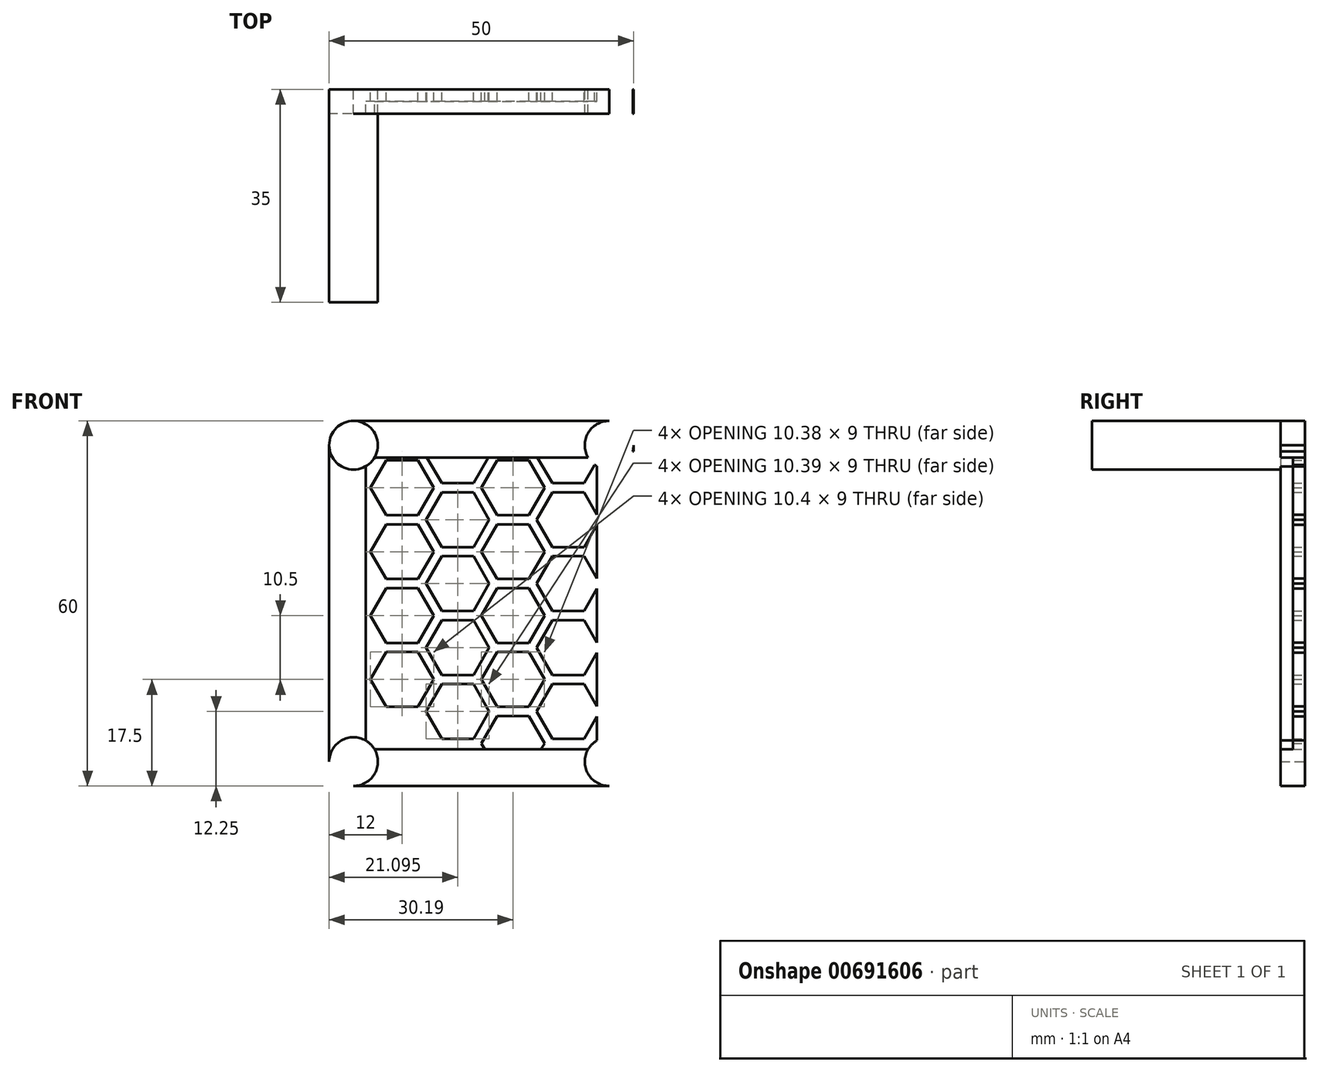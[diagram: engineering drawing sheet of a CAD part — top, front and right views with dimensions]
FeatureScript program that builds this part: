
annotation { "Feature Type Name" : "Feature", "Feature Type Description" : "" }
export const myFeature = defineFeature(function(context is Context, id is Id, definition is map)
    precondition{}
    {
        {
            var Q0;
            Q0=qCreatedBy(makeId("Front.planeOp"),FACE);
            var sketch = newSketch(context, id + "F0", { "sketchPlane" : qUnion([Q0])});
            skLineSegment(sketch, "E0.bottom", {"start": v(-21, 30) * mm, "end": v(21, 30) * mm});
            skLineSegment(sketch, "E0.top", {"start": v(-21, -30) * mm, "end": v(21, -30) * mm});
            skLineSegment(sketch, "E0.left", {"start": v(-25, 26) * mm, "end": v(-25, -26) * mm});
            skLineSegment(sketch, "E0.right", {"start": v(25, 26) * mm, "end": v(25, -26) * mm});
            skPoint(sketch, "E0.middle", {"position": v(0, 0) * mm});
            skCircle(sketch, "E1", {"center": v(-21, 26) * mm, "radius": 4 * mm});
            skPoint(sketch, "E2.visualSharp", {"position": v(-25, 30) * mm});
            skArc(sketch, "E2.filletArc", {"start": v(-21, 30) * mm, "mid": v(-23.83, 28.83) * mm, "end": v(-25, 26) * mm});
            skPoint(sketch, "E3.visualSharp", {"position": v(25, 30) * mm});
            skArc(sketch, "E3.filletArc", {"start": v(25, 26) * mm, "mid": v(23.83, 28.83) * mm, "end": v(21, 30) * mm});
            skPoint(sketch, "E4.visualSharp", {"position": v(25, -30) * mm});
            skArc(sketch, "E4.filletArc", {"start": v(21, -30) * mm, "mid": v(23.83, -28.83) * mm, "end": v(25, -26) * mm});
            skPoint(sketch, "E5.visualSharp", {"position": v(-25, -30) * mm});
            skArc(sketch, "E5.filletArc", {"start": v(-25, -26) * mm, "mid": v(-23.83, -28.83) * mm, "end": v(-21, -30) * mm});
            skLineSegment(sketch, "E6", {"start": v(-17.54, 24) * mm, "end": v(17.54, 24) * mm});
            skLineSegment(sketch, "E7", {"start": v(-17.54, -24) * mm, "end": v(17.54, -24) * mm});
            skLineSegment(sketch, "E8", {"start": v(19, 22.54) * mm, "end": v(19, -22.54) * mm});
            skLineSegment(sketch, "E9", {"start": v(-19, 22.54) * mm, "end": v(-19, -22.54) * mm});
            skCircle(sketch, "E10.cCircle", {"center": v(-13, 19) * mm, "radius": 4.5 * mm, "construction": true});
            skLineSegment(sketch, "E10.0", {"start": v(-7.8, 19) * mm, "end": v(-10.4, 14.5) * mm});
            skLineSegment(sketch, "E10.1", {"start": v(-10.4, 14.5) * mm, "end": v(-15.6, 14.5) * mm});
            skLineSegment(sketch, "E10.2", {"start": v(-15.6, 14.5) * mm, "end": v(-18.2, 19) * mm});
            skLineSegment(sketch, "E10.3", {"start": v(-18.2, 19) * mm, "end": v(-15.6, 23.5) * mm});
            skLineSegment(sketch, "E10.4", {"start": v(-15.6, 23.5) * mm, "end": v(-10.4, 23.5) * mm});
            skLineSegment(sketch, "E10.5", {"start": v(-10.4, 23.5) * mm, "end": v(-7.8, 19) * mm});
            skPoint(sketch, "E10.0.midPoint", {"position": v(-9.1, 16.75) * mm});
            skLineSegment(sketch, "E11.0.1.0", {"start": v(-10.4, 4) * mm, "end": v(-15.6, 4) * mm});
            skLineSegment(sketch, "E11.0.1.1", {"start": v(-7.8, 8.5) * mm, "end": v(-10.4, 4) * mm});
            skLineSegment(sketch, "E11.0.1.2", {"start": v(-10.4, 13) * mm, "end": v(-7.8, 8.5) * mm});
            skLineSegment(sketch, "E11.0.1.3", {"start": v(-15.6, 13) * mm, "end": v(-10.4, 13) * mm});
            skLineSegment(sketch, "E11.0.1.4", {"start": v(-18.2, 8.5) * mm, "end": v(-15.6, 13) * mm});
            skLineSegment(sketch, "E11.0.1.5", {"start": v(-15.6, 4) * mm, "end": v(-18.2, 8.5) * mm});
            skLineSegment(sketch, "E11.0.2.0", {"start": v(-10.4, -6.5) * mm, "end": v(-15.6, -6.5) * mm});
            skLineSegment(sketch, "E11.0.2.1", {"start": v(-7.8, -2) * mm, "end": v(-10.4, -6.5) * mm});
            skLineSegment(sketch, "E11.0.2.2", {"start": v(-10.4, 2.5) * mm, "end": v(-7.8, -2) * mm});
            skLineSegment(sketch, "E11.0.2.3", {"start": v(-15.6, 2.5) * mm, "end": v(-10.4, 2.5) * mm});
            skLineSegment(sketch, "E11.0.2.4", {"start": v(-18.2, -2) * mm, "end": v(-15.6, 2.5) * mm});
            skLineSegment(sketch, "E11.0.2.5", {"start": v(-15.6, -6.5) * mm, "end": v(-18.2, -2) * mm});
            skLineSegment(sketch, "E11.0.3.0", {"start": v(-10.4, -17) * mm, "end": v(-15.6, -17) * mm});
            skLineSegment(sketch, "E11.0.3.1", {"start": v(-7.8, -12.5) * mm, "end": v(-10.4, -17) * mm});
            skLineSegment(sketch, "E11.0.3.2", {"start": v(-10.4, -8) * mm, "end": v(-7.8, -12.5) * mm});
            skLineSegment(sketch, "E11.0.3.3", {"start": v(-15.6, -8) * mm, "end": v(-10.4, -8) * mm});
            skLineSegment(sketch, "E11.0.3.4", {"start": v(-18.2, -12.5) * mm, "end": v(-15.6, -8) * mm});
            skLineSegment(sketch, "E11.0.3.5", {"start": v(-15.6, -17) * mm, "end": v(-18.2, -12.5) * mm});
            skLineSegment(sketch, "E11.0.4.1", {"start": v(-7.8, -23) * mm, "end": v(-10.4, -27.5) * mm});
            skLineSegment(sketch, "E11.0.4.2", {"start": v(-10.4, -18.5) * mm, "end": v(-7.8, -23) * mm});
            skLineSegment(sketch, "E11.0.4.3", {"start": v(-15.6, -18.5) * mm, "end": v(-10.4, -18.5) * mm});
            skLineSegment(sketch, "E11.0.4.4", {"start": v(-18.2, -23) * mm, "end": v(-15.6, -18.5) * mm});
            skLineSegment(sketch, "E11.1.0.0", {"start": v(-1.3, 19.75) * mm, "end": v(-6.5, 19.75) * mm});
            skLineSegment(sketch, "E11.1.0.1", {"start": v(1.29, 24.25) * mm, "end": v(-1.3, 19.75) * mm});
            skLineSegment(sketch, "E11.1.0.5", {"start": v(-6.5, 19.75) * mm, "end": v(-9.1, 24.25) * mm});
            skLineSegment(sketch, "E11.1.1.0", {"start": v(-1.3, 9.25) * mm, "end": v(-6.5, 9.25) * mm});
            skLineSegment(sketch, "E11.1.1.1", {"start": v(1.29, 13.75) * mm, "end": v(-1.3, 9.25) * mm});
            skLineSegment(sketch, "E11.1.1.2", {"start": v(-1.3, 18.25) * mm, "end": v(1.29, 13.75) * mm});
            skLineSegment(sketch, "E11.1.1.3", {"start": v(-6.5, 18.25) * mm, "end": v(-1.3, 18.25) * mm});
            skLineSegment(sketch, "E11.1.1.4", {"start": v(-9.1, 13.75) * mm, "end": v(-6.5, 18.25) * mm});
            skLineSegment(sketch, "E11.1.1.5", {"start": v(-6.5, 9.25) * mm, "end": v(-9.1, 13.75) * mm});
            skLineSegment(sketch, "E11.1.2.0", {"start": v(-1.3, -1.25) * mm, "end": v(-6.5, -1.25) * mm});
            skLineSegment(sketch, "E11.1.2.1", {"start": v(1.29, 3.25) * mm, "end": v(-1.3, -1.25) * mm});
            skLineSegment(sketch, "E11.1.2.2", {"start": v(-1.3, 7.75) * mm, "end": v(1.29, 3.25) * mm});
            skLineSegment(sketch, "E11.1.2.3", {"start": v(-6.5, 7.75) * mm, "end": v(-1.3, 7.75) * mm});
            skLineSegment(sketch, "E11.1.2.4", {"start": v(-9.1, 3.25) * mm, "end": v(-6.5, 7.75) * mm});
            skLineSegment(sketch, "E11.1.2.5", {"start": v(-6.5, -1.25) * mm, "end": v(-9.1, 3.25) * mm});
            skLineSegment(sketch, "E11.1.3.0", {"start": v(-1.3, -11.75) * mm, "end": v(-6.5, -11.75) * mm});
            skLineSegment(sketch, "E11.1.3.1", {"start": v(1.29, -7.25) * mm, "end": v(-1.3, -11.75) * mm});
            skLineSegment(sketch, "E11.1.3.2", {"start": v(-1.3, -2.75) * mm, "end": v(1.29, -7.25) * mm});
            skLineSegment(sketch, "E11.1.3.3", {"start": v(-6.5, -2.75) * mm, "end": v(-1.3, -2.75) * mm});
            skLineSegment(sketch, "E11.1.3.4", {"start": v(-9.1, -7.25) * mm, "end": v(-6.5, -2.75) * mm});
            skLineSegment(sketch, "E11.1.3.5", {"start": v(-6.5, -11.75) * mm, "end": v(-9.1, -7.25) * mm});
            skLineSegment(sketch, "E11.1.4.0", {"start": v(-1.3, -22.25) * mm, "end": v(-6.5, -22.25) * mm});
            skLineSegment(sketch, "E11.1.4.1", {"start": v(1.29, -17.75) * mm, "end": v(-1.3, -22.25) * mm});
            skLineSegment(sketch, "E11.1.4.2", {"start": v(-1.3, -13.25) * mm, "end": v(1.29, -17.75) * mm});
            skLineSegment(sketch, "E11.1.4.3", {"start": v(-6.5, -13.25) * mm, "end": v(-1.3, -13.25) * mm});
            skLineSegment(sketch, "E11.1.4.4", {"start": v(-9.1, -17.75) * mm, "end": v(-6.5, -13.25) * mm});
            skLineSegment(sketch, "E11.1.4.5", {"start": v(-6.5, -22.25) * mm, "end": v(-9.1, -17.75) * mm});
            skLineSegment(sketch, "E11.2.1.0", {"start": v(7.78, 14.5) * mm, "end": v(2.59, 14.5) * mm});
            skLineSegment(sketch, "E11.2.1.1", {"start": v(10.38, 19) * mm, "end": v(7.78, 14.5) * mm});
            skLineSegment(sketch, "E11.2.1.2", {"start": v(7.78, 23.5) * mm, "end": v(10.38, 19) * mm});
            skLineSegment(sketch, "E11.2.1.3", {"start": v(2.59, 23.5) * mm, "end": v(7.78, 23.5) * mm});
            skLineSegment(sketch, "E11.2.1.4", {"start": v(0, 19) * mm, "end": v(2.59, 23.5) * mm});
            skLineSegment(sketch, "E11.2.1.5", {"start": v(2.59, 14.5) * mm, "end": v(0, 19) * mm});
            skLineSegment(sketch, "E11.2.2.0", {"start": v(7.78, 4) * mm, "end": v(2.59, 4) * mm});
            skLineSegment(sketch, "E11.2.2.1", {"start": v(10.38, 8.5) * mm, "end": v(7.78, 4) * mm});
            skLineSegment(sketch, "E11.2.2.2", {"start": v(7.78, 13) * mm, "end": v(10.38, 8.5) * mm});
            skLineSegment(sketch, "E11.2.2.3", {"start": v(2.59, 13) * mm, "end": v(7.78, 13) * mm});
            skLineSegment(sketch, "E11.2.2.4", {"start": v(0, 8.5) * mm, "end": v(2.59, 13) * mm});
            skLineSegment(sketch, "E11.2.2.5", {"start": v(2.59, 4) * mm, "end": v(0, 8.5) * mm});
            skLineSegment(sketch, "E11.2.3.0", {"start": v(7.78, -6.5) * mm, "end": v(2.59, -6.5) * mm});
            skLineSegment(sketch, "E11.2.3.1", {"start": v(10.38, -2) * mm, "end": v(7.78, -6.5) * mm});
            skLineSegment(sketch, "E11.2.3.2", {"start": v(7.78, 2.5) * mm, "end": v(10.38, -2) * mm});
            skLineSegment(sketch, "E11.2.3.3", {"start": v(2.59, 2.5) * mm, "end": v(7.78, 2.5) * mm});
            skLineSegment(sketch, "E11.2.3.4", {"start": v(0, -2) * mm, "end": v(2.59, 2.5) * mm});
            skLineSegment(sketch, "E11.2.3.5", {"start": v(2.59, -6.5) * mm, "end": v(0, -2) * mm});
            skLineSegment(sketch, "E11.2.4.0", {"start": v(7.78, -17) * mm, "end": v(2.59, -17) * mm});
            skLineSegment(sketch, "E11.2.4.1", {"start": v(10.38, -12.5) * mm, "end": v(7.78, -17) * mm});
            skLineSegment(sketch, "E11.2.4.2", {"start": v(7.78, -8) * mm, "end": v(10.38, -12.5) * mm});
            skLineSegment(sketch, "E11.2.4.3", {"start": v(2.59, -8) * mm, "end": v(7.78, -8) * mm});
            skLineSegment(sketch, "E11.2.4.4", {"start": v(0, -12.5) * mm, "end": v(2.59, -8) * mm});
            skLineSegment(sketch, "E11.2.4.5", {"start": v(2.59, -17) * mm, "end": v(0, -12.5) * mm});
            skLineSegment(sketch, "E11.2.5.1", {"start": v(10.38, -23) * mm, "end": v(7.78, -27.5) * mm});
            skLineSegment(sketch, "E11.2.5.2", {"start": v(7.78, -18.5) * mm, "end": v(10.38, -23) * mm});
            skLineSegment(sketch, "E11.2.5.3", {"start": v(2.59, -18.5) * mm, "end": v(7.78, -18.5) * mm});
            skLineSegment(sketch, "E11.2.5.4", {"start": v(0, -23) * mm, "end": v(2.59, -18.5) * mm});
            skLineSegment(sketch, "E11.2.5.5", {"start": v(2.59, -27.5) * mm, "end": v(0, -23) * mm});
            skLineSegment(sketch, "E11.direction1", {"start": v(-15.6, 14.5) * mm, "end": v(-6.5, 19.75) * mm, "construction": true});
            skLineSegment(sketch, "E11.direction2", {"start": v(-15.6, 14.5) * mm, "end": v(-15.6, 4) * mm, "construction": true});
            skLineSegment(sketch, "E12.0.3.1", {"start": v(16.88, 19.75) * mm, "end": v(11.68, 19.75) * mm});
            skLineSegment(sketch, "E12.3.3.1", {"start": v(19.48, 24.25) * mm, "end": v(16.88, 19.75) * mm});
            skLineSegment(sketch, "E12.15.3.1", {"start": v(11.68, 19.75) * mm, "end": v(9.08, 24.25) * mm});
            skLineSegment(sketch, "E12.0.3.2", {"start": v(16.88, 9.25) * mm, "end": v(11.68, 9.25) * mm});
            skLineSegment(sketch, "E12.3.3.2", {"start": v(19.48, 13.75) * mm, "end": v(16.88, 9.25) * mm});
            skLineSegment(sketch, "E12.6.3.2", {"start": v(16.88, 18.25) * mm, "end": v(19.48, 13.75) * mm});
            skLineSegment(sketch, "E12.9.3.2", {"start": v(11.68, 18.25) * mm, "end": v(16.88, 18.25) * mm});
            skLineSegment(sketch, "E12.12.3.2", {"start": v(9.08, 13.75) * mm, "end": v(11.68, 18.25) * mm});
            skLineSegment(sketch, "E12.15.3.2", {"start": v(11.68, 9.25) * mm, "end": v(9.08, 13.75) * mm});
            skLineSegment(sketch, "E12.0.3.3", {"start": v(16.88, -1.25) * mm, "end": v(11.68, -1.25) * mm});
            skLineSegment(sketch, "E12.3.3.3", {"start": v(19.48, 3.25) * mm, "end": v(16.88, -1.25) * mm});
            skLineSegment(sketch, "E12.6.3.3", {"start": v(16.88, 7.75) * mm, "end": v(19.48, 3.25) * mm});
            skLineSegment(sketch, "E12.9.3.3", {"start": v(11.68, 7.75) * mm, "end": v(16.88, 7.75) * mm});
            skLineSegment(sketch, "E12.12.3.3", {"start": v(9.08, 3.25) * mm, "end": v(11.68, 7.75) * mm});
            skLineSegment(sketch, "E12.15.3.3", {"start": v(11.68, -1.25) * mm, "end": v(9.08, 3.25) * mm});
            skLineSegment(sketch, "E12.0.3.4", {"start": v(16.88, -11.75) * mm, "end": v(11.68, -11.75) * mm});
            skLineSegment(sketch, "E12.3.3.4", {"start": v(19.48, -7.25) * mm, "end": v(16.88, -11.75) * mm});
            skLineSegment(sketch, "E12.6.3.4", {"start": v(16.88, -2.75) * mm, "end": v(19.48, -7.25) * mm});
            skLineSegment(sketch, "E12.9.3.4", {"start": v(11.68, -2.75) * mm, "end": v(16.88, -2.75) * mm});
            skLineSegment(sketch, "E12.12.3.4", {"start": v(9.08, -7.25) * mm, "end": v(11.68, -2.75) * mm});
            skLineSegment(sketch, "E12.15.3.4", {"start": v(11.68, -11.75) * mm, "end": v(9.08, -7.25) * mm});
            skLineSegment(sketch, "E12.0.3.5", {"start": v(16.88, -22.25) * mm, "end": v(11.68, -22.25) * mm});
            skLineSegment(sketch, "E12.3.3.5", {"start": v(19.48, -17.75) * mm, "end": v(16.88, -22.25) * mm});
            skLineSegment(sketch, "E12.6.3.5", {"start": v(16.88, -13.25) * mm, "end": v(19.48, -17.75) * mm});
            skLineSegment(sketch, "E12.9.3.5", {"start": v(11.68, -13.25) * mm, "end": v(16.88, -13.25) * mm});
            skLineSegment(sketch, "E12.12.3.5", {"start": v(9.08, -17.75) * mm, "end": v(11.68, -13.25) * mm});
            skLineSegment(sketch, "E12.15.3.5", {"start": v(11.68, -22.25) * mm, "end": v(9.08, -17.75) * mm});
            skLineSegment(sketch, "E12.9.4.0", {"start": v(20.77, 44.5) * mm, "end": v(25.97, 44.5) * mm});
            skLineSegment(sketch, "E12.0.4.1", {"start": v(25.97, 25) * mm, "end": v(20.77, 25) * mm});
            skLineSegment(sketch, "E13", {"start": v(0, 40.96) * mm, "end": v(0, -40.98) * mm, "construction": true});
            skLineSegment(sketch, "E14", {"start": v(-42.2, 0) * mm, "end": v(47.65, 0) * mm, "construction": true});
            skCircle(sketch, "E15.MirrorC", {"center": v(21, 26) * mm, "radius": 4 * mm});
            skCircle(sketch, "E16.MirrorC", {"center": v(-21, -26) * mm, "radius": 4 * mm});
            skCircle(sketch, "E17.MirrorC", {"center": v(21, -26) * mm, "radius": 4 * mm});
            skSolve(sketch);
        }
        {
            var Q0;
            {var subQ3=sQuery(id+"F0.wireOp",EDGE,"E6");Q0=makeQuery(id+"F0.imprint","IMPRINT",FACE,{"disambiguationData":[TD([[makeQuery(id+"F0.imprint","IMPRINT",EDGE,{"derivedFrom":subQ3}),-1.0]])]});}
            extrude(context, id + "F1", {"entities" : qUnion([Q0]), "depth" : 2 * mm, "offsetDistance" : 25 * mm});
        }
        {
            var Q0;
            {var subQ0=sQuery(id+"F0.wireOp",EDGE,"E0.right");Q0=makeQuery(id+"F0.imprint","IMPRINT",FACE,{"disambiguationData":[TD([[makeQuery(id+"F0.imprint","IMPRINT",EDGE,{"derivedFrom":subQ0}),-1.0]])]});}
            var Q1;
            {var subQ0=sQuery(id+"F0.wireOp",EDGE,"E0.bottom");Q1=makeQuery(id+"F0.imprint","IMPRINT",FACE,{"disambiguationData":[TD([[makeQuery(id+"F0.imprint","IMPRINT",EDGE,{"derivedFrom":subQ0}),-1.0]])]});}
            var Q2;
            {var subQ0=sQuery(id+"F0.wireOp",EDGE,"E0.left");Q2=makeQuery(id+"F0.imprint","IMPRINT",FACE,{"disambiguationData":[TD([[makeQuery(id+"F0.imprint","IMPRINT",EDGE,{"derivedFrom":subQ0}),1.0]])]});}
            var Q3;
            {var subQ0=sQuery(id+"F0.wireOp",EDGE,"E0.top");Q3=makeQuery(id+"F0.imprint","IMPRINT",FACE,{"disambiguationData":[TD([[makeQuery(id+"F0.imprint","IMPRINT",EDGE,{"derivedFrom":subQ0}),1.0]])]});}
            extrude(context, id + "F2", {"entities" : qUnion([Q0, Q1, Q2, Q3]), "operationType" : NewBodyOperationType.ADD, "depth" : 4 * mm, "offsetDistance" : 25 * mm});
        }
        {
            var Q0;
            {var subQ0=sQuery(id+"F0.wireOp",EDGE,"E1");var subQ1=makeQuery(id+"F0.imprint","INTERSECT",VERTEX,{"derivedFrom":[sQuery(id+"F0.wireOp",EDGE,"E0.bottom"),subQ0]});Q0=makeQuery(id+"F0.imprint","IMPRINT",FACE,{"disambiguationData":[TD([[makeQuery(id+"F0.imprint","IMPRINT",EDGE,{"disambiguationData":[TD([[subQ1,-1.0]])],"derivedFrom":subQ0}),1.0]])]});}
            var Q1;
            {var subQ0=sQuery(id+"F0.wireOp",EDGE,"83018fb1-80dc-4c40-ab42-aaf559f4c7fc.1.1.0");var subQ1=makeQuery(id+"F0.imprint","INTERSECT",VERTEX,{"derivedFrom":[sQuery(id+"F0.wireOp",EDGE,"E0.right"),subQ0]});Q1=makeQuery(id+"F0.imprint","IMPRINT",FACE,{"disambiguationData":[TD([[makeQuery(id+"F0.imprint","IMPRINT",EDGE,{"disambiguationData":[TD([[subQ1,-1.0]])],"derivedFrom":subQ0}),1.0]])]});}
            var Q2;
            {var subQ0=sQuery(id+"F0.wireOp",EDGE,"83018fb1-80dc-4c40-ab42-aaf559f4c7fc.1.0.0");var subQ1=makeQuery(id+"F0.imprint","INTERSECT",VERTEX,{"derivedFrom":[sQuery(id+"F0.wireOp",EDGE,"E0.bottom"),subQ0]});Q2=makeQuery(id+"F0.imprint","IMPRINT",FACE,{"disambiguationData":[TD([[makeQuery(id+"F0.imprint","IMPRINT",EDGE,{"disambiguationData":[TD([[subQ1,1.0]])],"derivedFrom":subQ0}),1.0]])]});}
            var Q3;
            {var subQ0=sQuery(id+"F0.wireOp",EDGE,"83018fb1-80dc-4c40-ab42-aaf559f4c7fc.0.1.0");var subQ1=makeQuery(id+"F0.imprint","INTERSECT",VERTEX,{"derivedFrom":[subQ0,sQuery(id+"F0.wireOp",EDGE,"E7")]});Q3=makeQuery(id+"F0.imprint","IMPRINT",FACE,{"disambiguationData":[TD([[makeQuery(id+"F0.imprint","IMPRINT",EDGE,{"disambiguationData":[TD([[subQ1,-1.0]])],"derivedFrom":subQ0}),1.0]])]});}
            extrude(context, id + "F3", {"entities" : qUnion([Q0, Q1, Q2, Q3]), "operationType" : NewBodyOperationType.ADD, "depth" : 35 * mm, "offsetDistance" : 25 * mm});
        }
        {
            var Q0;
            Q0=sQuery(id+"F0.wireOp",VERTEX,"E4.filletArc.center");
            var Q1;
            Q1=makeQuery(id+"F1.opExtrude","SWEPT_BODY",BODY,{"disambiguationData":[OSD([sQuery(id+"F0.wireOp",EDGE,"E1"),sQuery(id+"F0.wireOp",EDGE,"83018fb1-80dc-4c40-ab42-aaf559f4c7fc.0.1.0"),sQuery(id+"F0.wireOp",EDGE,"83018fb1-80dc-4c40-ab42-aaf559f4c7fc.1.0.0"),sQuery(id+"F0.wireOp",EDGE,"83018fb1-80dc-4c40-ab42-aaf559f4c7fc.1.1.0"),sQuery(id+"F0.wireOp",EDGE,"E6"),sQuery(id+"F0.wireOp",EDGE,"E7"),sQuery(id+"F0.wireOp",EDGE,"E8"),sQuery(id+"F0.wireOp",EDGE,"E9")])]});
            hole(context, id + "F4", {"style" : HoleStyle.SIMPLE, "endStyle" : HoleEndStyle.BLIND, "oppositeDirection" : true, "holeDiameter" : 3.5 * mm, "majorDiameter" : 5 * mm, "holeDepth" : 25 * mm, "isTappedThrough" : true, "tappedDepth" : 12 * mm, "tapClearance" : 3, "startFromSketch" : true, "locations" : qUnion([Q0]), "scope" : qUnion([Q1])});
        }
    });
